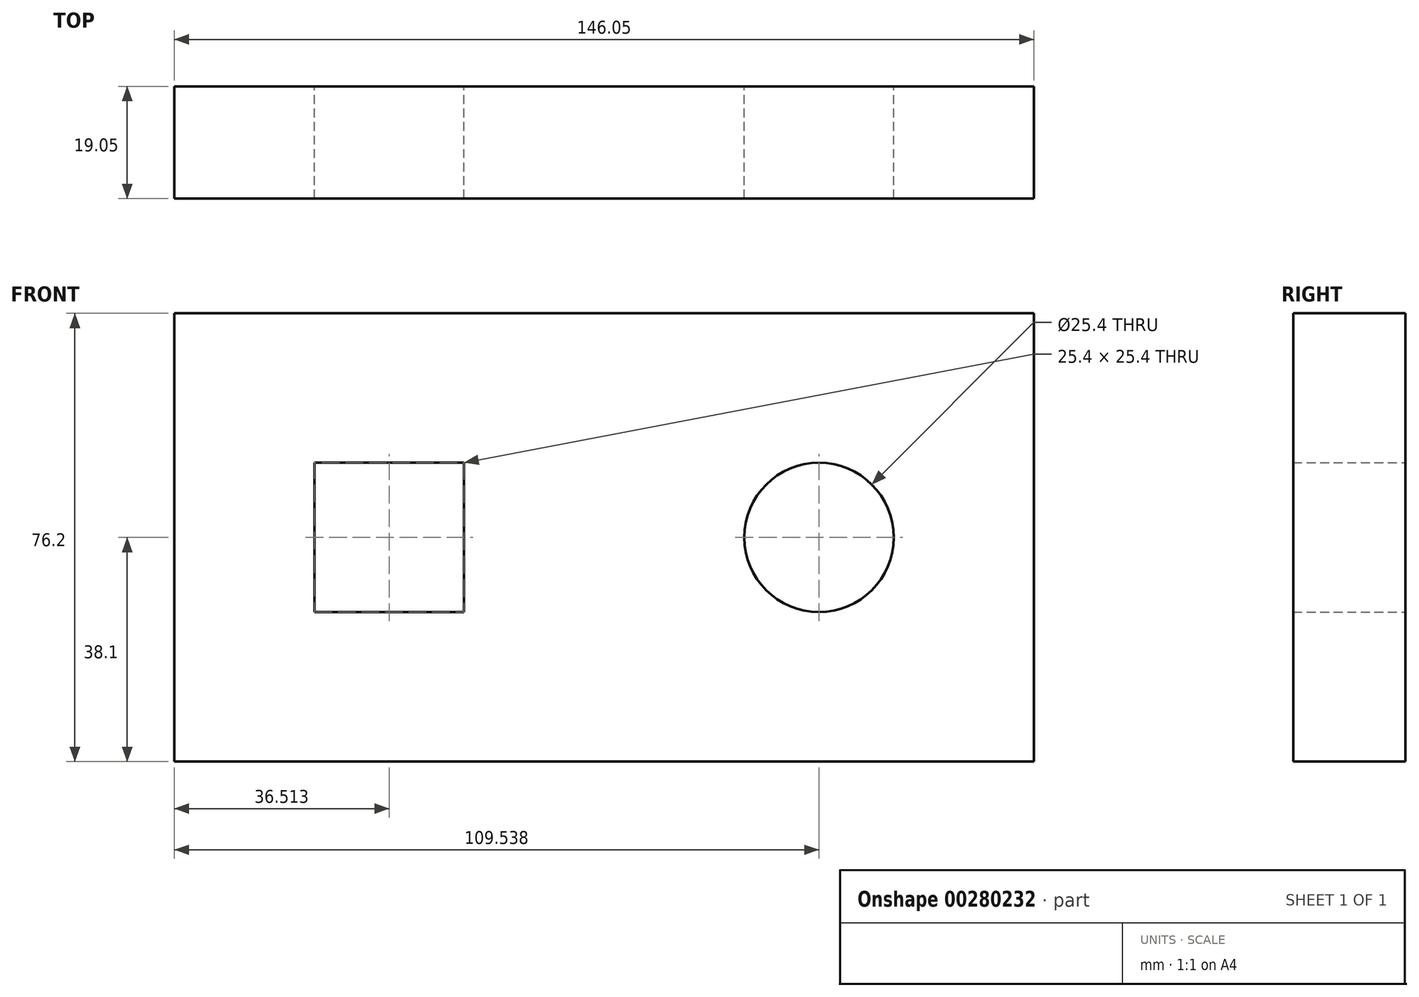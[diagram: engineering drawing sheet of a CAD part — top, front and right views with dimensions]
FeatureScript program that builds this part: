
annotation { "Feature Type Name" : "Feature", "Feature Type Description" : "" }
export const myFeature = defineFeature(function(context is Context, id is Id, definition is map)
    precondition{}
    {
        {
            var Q0;
            Q0=qCreatedBy(makeId("Front.planeOp"),FACE);
            var sketch = newSketch(context, id + "F0", { "sketchPlane" : qUnion([Q0])});
            skLineSegment(sketch, "E0.bottom", {"start": v(0, 0) * mm, "end": v(-146.05, 0) * mm});
            skLineSegment(sketch, "E0.top", {"start": v(0, 76.2) * mm, "end": v(-146.05, 76.2) * mm});
            skLineSegment(sketch, "E0.left", {"start": v(0, 0) * mm, "end": v(0, 76.2) * mm});
            skLineSegment(sketch, "E0.right", {"start": v(-146.05, 0) * mm, "end": v(-146.05, 76.2) * mm});
            skLineSegment(sketch, "E1.bottom", {"start": v(-96.84, 25.4) * mm, "end": v(-122.24, 25.4) * mm});
            skLineSegment(sketch, "E1.top", {"start": v(-96.84, 50.8) * mm, "end": v(-122.24, 50.8) * mm});
            skLineSegment(sketch, "E1.left", {"start": v(-96.84, 25.4) * mm, "end": v(-96.84, 50.8) * mm});
            skLineSegment(sketch, "E1.right", {"start": v(-122.24, 25.4) * mm, "end": v(-122.24, 50.8) * mm});
            skCircle(sketch, "E2", {"center": v(-36.51, 38.1) * mm, "radius": 12.7 * mm});
            skSolve(sketch);
        }
        {
            var Q0;
            Q0=makeQuery(id+"F0.imprint","IMPRINT",FACE,{"disambiguationData":[TD([[makeQuery(id+"F0.imprint","IMPRINT",EDGE,{"derivedFrom":sQuery(id+"F0.wireOp",EDGE,"E0.bottom")}),-1.0]])]});
            extrude(context, id + "F1", {"entities" : qUnion([Q0]), "depth" : 19.05 * mm});
        }
    });
